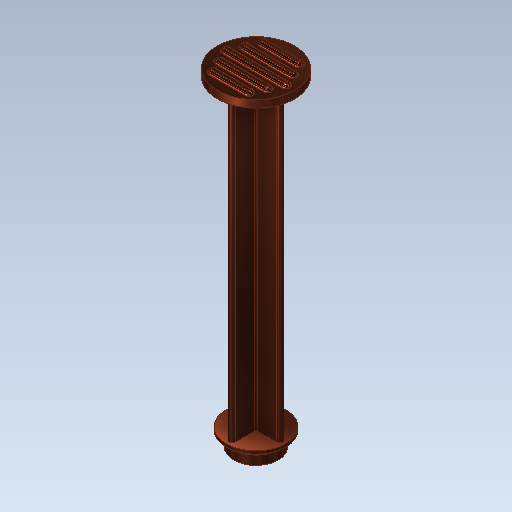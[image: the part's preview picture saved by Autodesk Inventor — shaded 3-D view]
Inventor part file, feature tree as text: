
AUTODESK INVENTOR PART (.ipt)
format: ipt  version: 2020 (Build 240168000, 168)  size: 221,696 bytes
history: native  units: mm
features: sketch x4, extrude x3, revolve x1, fillet x1
ambient origin geometry x8: Origin, YZ Plane, XZ Plane, XY Plane, X Axis, Y Axis, Z Axis, Center Point
bodies: Solid1 (feature_tree)
feature tree (9):
  revolve  "Revolution1"  [1 undecoded]
  extrude  "Extrusion1"  Depth=2.0mm
  extrude  "Extrusion2"  Depth=7.5mm
  extrude  "Extrusion3"  Depth=1.0mm
  fillet  "Fillet1"  Radius=1.0mm
  sketch  "Sketch1"  dims[d0=10.0mm d1=6.0mm]
  sketch  "Sketch2"  dims[d2=1.0mm d3=2.0mm]
  sketch  "Sketch3"  dims[d4=3.0mm d5=7.5mm]
  sketch  "Sketch4"  dims[d6=90.0deg d7=1.0mm d8=1.0mm d9=1.0mm d10=1.0mm d11=8.0mm d16=8.0mm d17=8.0mm d18=8.0mm d19=0.5mm d20=102.0mm d21=0.0mm d22=26.0mm d23=2.5mm d24=0.0mm d25=1.5mm d26=1.5mm d27=10.0mm d28=10.0mm d29=1.2mm d30=3.0mm d31=8.0mm d32=8.0mm d33=1.2mm d34=6.0mm d35=6.0mm d36=3.0mm d37=1.2mm d38=8.0mm d39=8.0mm d40=3.0mm d41=1.2mm d42=3.0mm d43=6.0mm d44=6.0mm d45=1.0mm d46=0.0mm d47=1.0mm]
note: 1 required parameter value undecoded (feature->parameter linkage not recoverable at this tier; creation-order binding heuristic only, values carry confidence <= 0.55)
